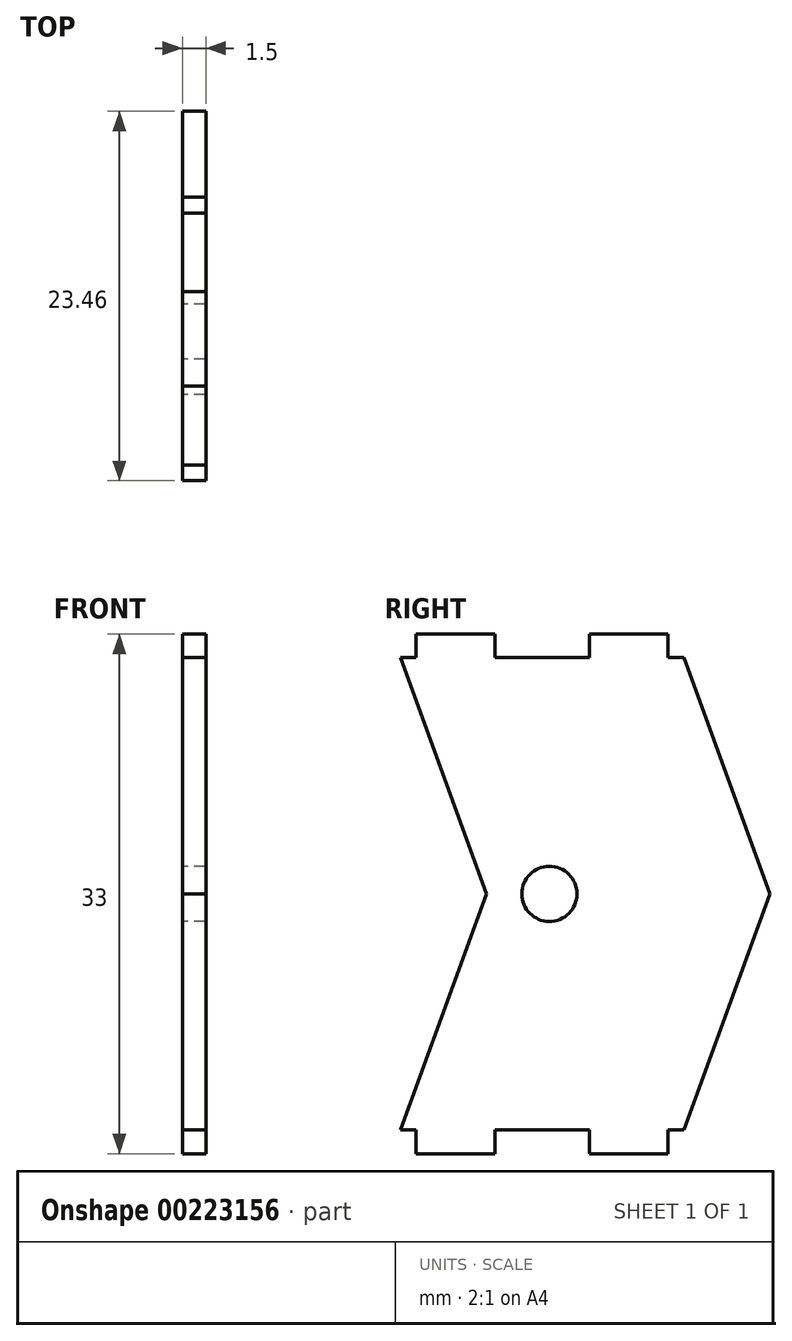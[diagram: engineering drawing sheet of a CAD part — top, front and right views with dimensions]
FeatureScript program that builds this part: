
annotation { "Feature Type Name" : "Feature", "Feature Type Description" : "" }
export const myFeature = defineFeature(function(context is Context, id is Id, definition is map)
    precondition{}
    {
        {
            var Q0;
            Q0=qCreatedBy(makeId("Right.planeOp"),FACE);
            var sketch = newSketch(context, id + "F0", { "sketchPlane" : qUnion([Q0])});
            skLineSegment(sketch, "E0", {"start": v(-3, 0) * mm, "end": v(3, 0) * mm});
            skLineSegment(sketch, "E1", {"start": v(3, 0) * mm, "end": v(3, -1.5) * mm});
            skLineSegment(sketch, "E2", {"start": v(3, -1.5) * mm, "end": v(8, -1.5) * mm});
            skLineSegment(sketch, "E3", {"start": v(8, -1.5) * mm, "end": v(8, 0) * mm});
            skLineSegment(sketch, "E4", {"start": v(8, 0) * mm, "end": v(9, 0) * mm});
            skLineSegment(sketch, "E5", {"start": v(9, 0) * mm, "end": v(14.46, 15) * mm});
            skLineSegment(sketch, "E6", {"start": v(-3.54, 15) * mm, "end": v(-9, 0) * mm});
            skLineSegment(sketch, "E7", {"start": v(-9, 0) * mm, "end": v(-8, 0) * mm});
            skLineSegment(sketch, "E8", {"start": v(-8, 0) * mm, "end": v(-8, -1.5) * mm});
            skLineSegment(sketch, "E9", {"start": v(-8, -1.5) * mm, "end": v(-3, -1.5) * mm});
            skLineSegment(sketch, "E10", {"start": v(-3, -1.5) * mm, "end": v(-3, 0) * mm});
            skLineSegment(sketch, "E11", {"start": v(-3.54, 15) * mm, "end": v(-9, 30) * mm});
            skLineSegment(sketch, "E12", {"start": v(-9, 30) * mm, "end": v(-8, 30) * mm});
            skLineSegment(sketch, "E13", {"start": v(-8, 30) * mm, "end": v(-8, 31.5) * mm});
            skLineSegment(sketch, "E14", {"start": v(-8, 31.5) * mm, "end": v(-3, 31.5) * mm});
            skLineSegment(sketch, "E15", {"start": v(-3, 31.5) * mm, "end": v(-3, 30) * mm});
            skLineSegment(sketch, "E16", {"start": v(-3, 30) * mm, "end": v(3, 30) * mm});
            skLineSegment(sketch, "E17", {"start": v(3, 30) * mm, "end": v(3, 31.5) * mm});
            skLineSegment(sketch, "E18", {"start": v(3, 31.5) * mm, "end": v(8, 31.5) * mm});
            skLineSegment(sketch, "E19", {"start": v(8, 31.5) * mm, "end": v(8, 30) * mm});
            skLineSegment(sketch, "E20", {"start": v(8, 30) * mm, "end": v(9, 30) * mm});
            skLineSegment(sketch, "E21", {"start": v(9, 30) * mm, "end": v(14.46, 15) * mm});
            skCircle(sketch, "E22", {"center": v(0.46, 15) * mm, "radius": 1.75 * mm});
            skSolve(sketch);
        }
        {
            var Q0;
            Q0 = qSketchRegion(id + "F0", true);
            extrude(context, id + "F1", {"entities" : qUnion([Q0]), "depth" : 1.5 * mm});
        }
    });
